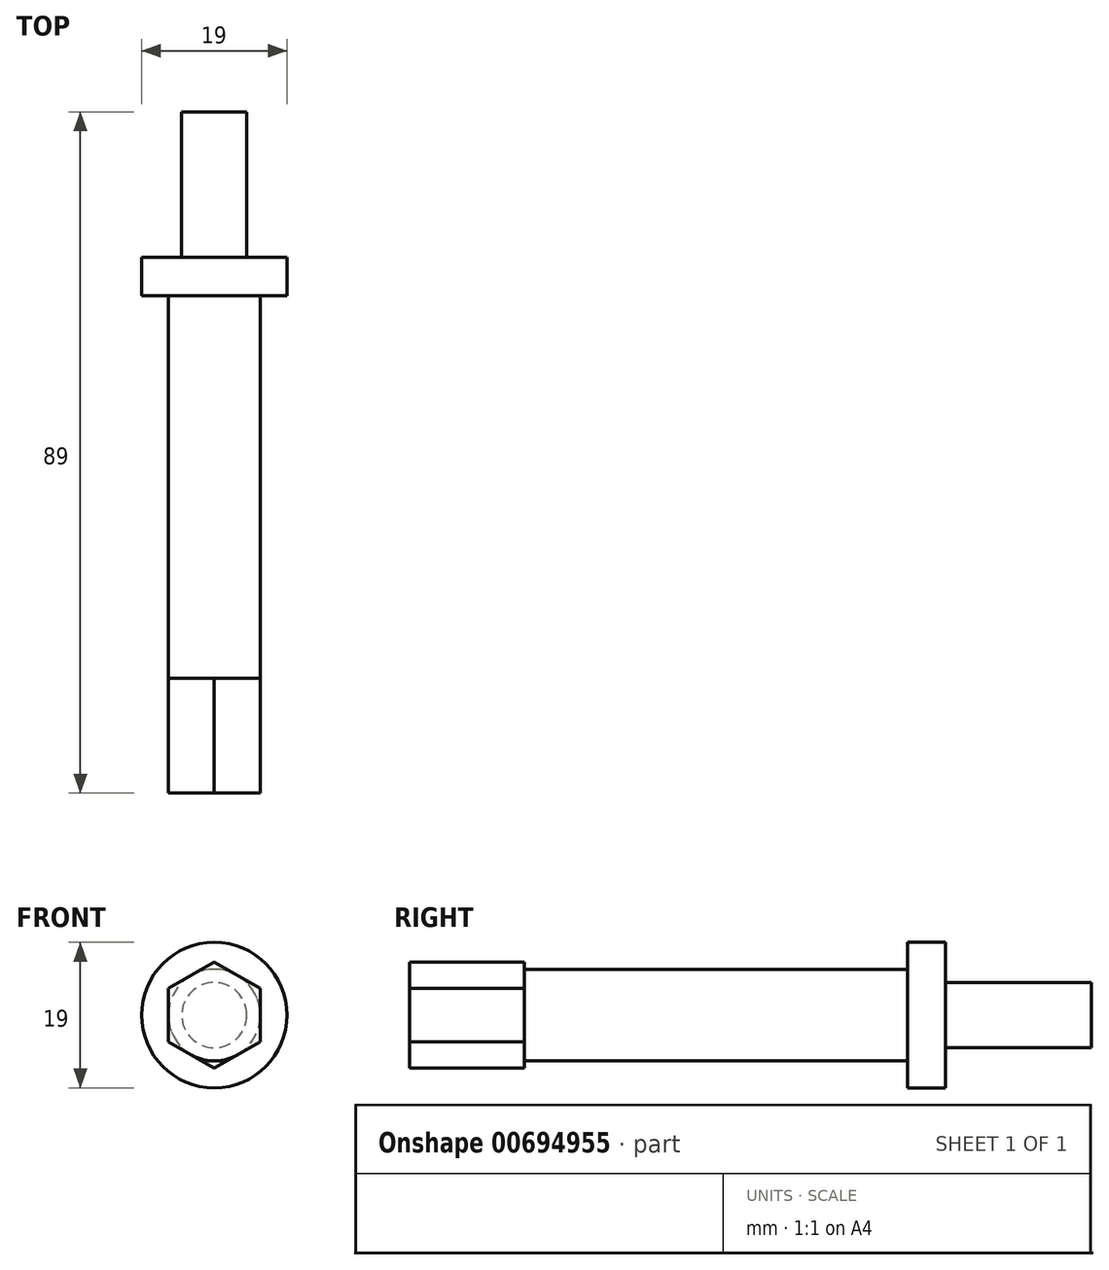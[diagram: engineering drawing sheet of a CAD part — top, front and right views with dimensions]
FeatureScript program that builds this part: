
annotation { "Feature Type Name" : "Feature", "Feature Type Description" : "" }
export const myFeature = defineFeature(function(context is Context, id is Id, definition is map)
    precondition{}
    {
        {
            var Q0;
            Q0=qCreatedBy(makeId("Front.planeOp"),FACE);
            var sketch = newSketch(context, id + "F0", { "sketchPlane" : qUnion([Q0])});
            skCircle(sketch, "E0", {"center": v(0, 0) * mm, "radius": 4.25 * mm});
            skSolve(sketch);
        }
        {
            var Q0;
            Q0=makeQuery(id+"F0.imprint","IMPRINT",FACE,{"disambiguationData":[TD([[makeQuery(id+"F0.imprint","IMPRINT",EDGE,{"derivedFrom":sQuery(id+"F0.wireOp",EDGE,"E0")}),1.0]])]});
            extrude(context, id + "F1", {"entities" : qUnion([Q0]), "depth" : 19 * mm, "offsetDistance" : 25 * mm});
        }
        {
            var Q0;
            Q0=makeQuery(id+"F1.opExtrude","CAP_FACE",FACE,{"disambiguationData":[OSD([sQuery(id+"F0.wireOp",EDGE,"E0")])],"isStart":false});
            var sketch = newSketch(context, id + "F2", { "sketchPlane" : qUnion([Q0])});
            skCircle(sketch, "E1", {"center": v(0, 0) * mm, "radius": 9.5 * mm});
            skSolve(sketch);
        }
        {
            var Q0;
            Q0=makeQuery(id+"F2.imprint","IMPRINT",FACE,{"disambiguationData":[TD([[makeQuery(id+"F2.imprint","IMPRINT",EDGE,{"derivedFrom":makeQuery(id+"F1.opExtrude","CAP_EDGE",EDGE,{"disambiguationData":[OSD([sQuery(id+"F0.wireOp",EDGE,"E0")])],"isStart":false})}),1.0]])]});
            var Q1;
            Q1=makeQuery(id+"F2.imprint","IMPRINT",FACE,{"disambiguationData":[TD([[makeQuery(id+"F2.imprint","IMPRINT",EDGE,{"derivedFrom":sQuery(id+"F2.wireOp",EDGE,"E1")}),1.0]])]});
            extrude(context, id + "F3", {"entities" : qUnion([Q0, Q1]), "operationType" : NewBodyOperationType.ADD, "depth" : 5 * mm, "offsetDistance" : 25 * mm});
        }
        {
            var Q0;
            Q0=makeQuery(id+"F3.opExtrude","CAP_FACE",FACE,{"disambiguationData":[OSD([sQuery(id+"F2.wireOp",EDGE,"E1")])],"isStart":false});
            var sketch = newSketch(context, id + "F4", { "sketchPlane" : qUnion([Q0])});
            skCircle(sketch, "E2", {"center": v(0, 0) * mm, "radius": 6 * mm});
            skSolve(sketch);
        }
        {
            var Q0;
            Q0=makeQuery(id+"F4.imprint","IMPRINT",FACE,{"disambiguationData":[TD([[makeQuery(id+"F4.imprint","IMPRINT",EDGE,{"derivedFrom":sQuery(id+"F4.wireOp",EDGE,"E2")}),1.0]])]});
            extrude(context, id + "F5", {"entities" : qUnion([Q0]), "operationType" : NewBodyOperationType.ADD, "depth" : 50 * mm, "offsetDistance" : 25 * mm});
        }
        {
            var Q0;
            Q0=makeQuery(id+"F5.opExtrude","CAP_FACE",FACE,{"disambiguationData":[OSD([sQuery(id+"F4.wireOp",EDGE,"E2")])],"isStart":false});
            var sketch = newSketch(context, id + "F6", { "sketchPlane" : qUnion([Q0])});
            skCircle(sketch, "E3.cCircle", {"center": v(0, 0) * mm, "radius": 6 * mm, "construction": true});
            skLineSegment(sketch, "E3.0", {"start": v(6, 3.46) * mm, "end": v(6, -3.46) * mm});
            skLineSegment(sketch, "E3.1", {"start": v(6, -3.46) * mm, "end": v(0, -6.93) * mm});
            skLineSegment(sketch, "E3.2", {"start": v(0, -6.93) * mm, "end": v(-6, -3.46) * mm});
            skLineSegment(sketch, "E3.3", {"start": v(-6, -3.46) * mm, "end": v(-6, 3.46) * mm});
            skLineSegment(sketch, "E3.4", {"start": v(-6, 3.46) * mm, "end": v(0, 6.93) * mm});
            skLineSegment(sketch, "E3.5", {"start": v(0, 6.93) * mm, "end": v(6, 3.46) * mm});
            skPoint(sketch, "E3.0.midPoint", {"position": v(6, 0) * mm});
            skSolve(sketch);
        }
        {
            var Q0;
            Q0 = qSketchRegion(id + "F6", true);
            extrude(context, id + "F7", {"entities" : qUnion([Q0]), "operationType" : NewBodyOperationType.ADD, "depth" : 15 * mm, "offsetDistance" : 25 * mm});
        }
    });
